# Revit family: Casement_41_G_Top_Hung_SD_Standard
name_source: partatom
category: Windows
revit_build: Autodesk Revit 2014 (Build: 20130308_1515(x64)
units: mm (PartAtom-declared; Revit-internal decimal feet)

## types (12) — shared parameters
Corrected Mullion Configuration = 2 mm  [stored 0.00656168 ft]
Custom Window Height = 1190 mm  [stored 3.9042 ft]
Description = Window 41mm, Type G, Top hung, Standard sash
Frame Profile Thickness = 41 mm  [stored 0.134514 ft]
Heavy Duty Sash = No
Limit Fixed Pane Height Max = 3000 mm  [stored 9.84252 ft]
Limit Fixed Pane Height Min = 200 mm  [stored 0.656168 ft]
Limit Fixed Pane Width Max = 3000 mm  [stored 9.84252 ft]
Limit Fixed Pane Width Min = 200 mm  [stored 0.656168 ft]
Limit Sash Height Max = 1200 mm  [stored 3.93701 ft]
Limit Sash Height Min = 300 mm  [stored 0.984252 ft]
Limit Sash Width Max = 1500 mm  [stored 4.92126 ft]
Limit Sash Width Min = 300 mm  [stored 0.984252 ft]
Manufacturer = Crealco
Max System DG Unit Thickness = 25 mm  [stored 0.082021 ft]
Model = Casement 41
Rough Width = 3 mm  [stored 0.00984252 ft]
Sash Side Gap = 44 mm
Standard Mullion Different = No
Standard Sash = Yes
URL = http://www.crealco.co.za
Wall Closure = By host
zero-valued in all types: Custom Frame Offset From Exterior

## per-type parameters (varying)
| type | Clearvue Insulated LowE SHGC Value | Clearvue Insulated LowE U Value | Clearvue Insulated SHGC Value | Clearvue Insulated U Value | Clearvue SHGC Value | Clearvue U Value | Custom Sash Width | Custom Windload | Custom Window Width | Energy Advantage SHGC Value | Energy Advantage U Value | Intruderprufe Insulated LowE SHGC Value | Intruderprufe Insulated LowE U Value | Intruderprufe Insulated SHGC Value | Intruderprufe Insulated U Value | Intruderprufe LowE SHGC Value | Intruderprufe LowE U Value | Intruderprufe SHGC Value | Intruderprufe U Value | Toughened Safety SHGC Value | Toughened Safety U Value |
| 41-1212DT-SD-1000Pa | 0.72 | 4.3 | 0.72 | 4.38 | 0.545 | 6.06 | 525 mm | 1000 mm  [stored 3.28084 ft] | 1190 mm  [stored 3.9042 ft] | 0.489 | 4.71 | 0.598 | 3.11 | 0.599 | 3.31 | 0.455 | 4.57 | 0.513 | 5.78 | 0.545 | 6.06 |
| 41-1212DT-SD-1500Pa | 0.72 | 4.3 | 0.72 | 4.38 | 0.545 | 6.06 | 525 mm | 1500 mm  [stored 4.92126 ft] | 1190 mm  [stored 3.9042 ft] | 0.489 | 4.71 | 0.598 | 3.11 | 0.599 | 3.31 | 0.455 | 4.57 | 0.513 | 5.78 | 0.545 | 6.06 |
| 41-1212DT-SD-2000Pa | 0.72 | 4.3 | 0.72 | 4.38 | 0.545 | 6.06 | 525 mm | 2000 mm  [stored 6.56168 ft] | 1190 mm  [stored 3.9042 ft] | 0.489 | 4.71 | 0.598 | 3.11 | 0.599 | 3.31 | 0.455 | 4.57 | 0.513 | 5.78 | 0.545 | 6.06 |
| 41-1512DT-SD-1000Pa | 0.746 | 4.49 | 0.746 | 4.55 | 0.591 | 6.04 | 525 mm | 1000 mm  [stored 3.28084 ft] | 1490 mm  [stored 4.88845 ft] | 0.53 | 4.58 | 0.62 | 3.13 | 0.62 | 3.3 | 0.492 | 4.43 | 0.556 | 5.77 | 0.591 | 6.04 |
| 41-1512DT-SD-1500Pa | 0.746 | 4.49 | 0.746 | 4.55 | 0.591 | 6.04 | 525 mm | 1500 mm  [stored 4.92126 ft] | 1490 mm  [stored 4.88845 ft] | 0.53 | 4.58 | 0.62 | 3.13 | 0.62 | 3.3 | 0.492 | 4.43 | 0.556 | 5.77 | 0.591 | 6.04 |
| 41-1512DT-SD-2000Pa | 0.746 | 4.49 | 0.746 | 4.55 | 0.591 | 6.04 | 525 mm | 2000 mm  [stored 6.56168 ft] | 1490 mm  [stored 4.88845 ft] | 0.53 | 4.58 | 0.62 | 3.13 | 0.62 | 3.3 | 0.492 | 4.43 | 0.556 | 5.77 | 0.591 | 6.04 |
| 41-1812DT-SD-1000Pa | 0.747 | 4.52 | 0.747 | 4.57 | 0.595 | 6.04 | 825 mm | 1000 mm  [stored 3.28084 ft] | 1790 mm  [stored 5.8727 ft] | 0.533 | 4.52 | 0.62 | 3.13 | 0.621 | 3.34 | 0.496 | 4.39 | 0.56 | 5.75 | 0.595 | 6.04 |
| 41-1812DT-SD-1500Pa | 0.747 | 4.52 | 0.747 | 4.57 | 0.595 | 6.04 | 825 mm | 1500 mm  [stored 4.92126 ft] | 1790 mm  [stored 5.8727 ft] | 0.533 | 4.52 | 0.62 | 3.13 | 0.621 | 3.34 | 0.496 | 4.39 | 0.56 | 5.75 | 0.595 | 6.04 |
| 41-1812DT-SD-2000Pa | 0.747 | 4.52 | 0.747 | 4.57 | 0.595 | 6.04 | 825 mm | 2000 mm  [stored 6.56168 ft] | 1790 mm  [stored 5.8727 ft] | 0.533 | 4.52 | 0.62 | 3.13 | 0.621 | 3.34 | 0.496 | 4.39 | 0.56 | 5.75 | 0.595 | 6.04 |
| 41-2412DT-SD-1000Pa | 0.773 | 4.7 | 0.773 | 4.74 | 0.639 | 6.02 | 825 mm | 1000 mm  [stored 3.28084 ft] | 2390 mm  [stored 7.84121 ft] | 0.572 | 4.4 | 0.641 | 3.16 | 0.642 | 3.32 | 0.532 | 4.26 | 0.601 | 5.75 | 0.639 | 6.02 |
| 41-2412DT-SD-1500Pa | 0.773 | 4.7 | 0.773 | 4.74 | 0.639 | 6.02 | 825 mm | 1500 mm  [stored 4.92126 ft] | 2390 mm  [stored 7.84121 ft] | 0.572 | 4.4 | 0.641 | 3.16 | 0.642 | 3.32 | 0.532 | 4.26 | 0.601 | 5.75 | 0.639 | 6.02 |
| 41-2412DT-SD-2000Pa | 0.773 | 4.7 | 0.773 | 4.74 | 0.639 | 6.02 | 825 mm | 2000 mm  [stored 6.56168 ft] | 2390 mm  [stored 7.84121 ft] | 0.572 | 4.4 | 0.641 | 3.16 | 0.642 | 3.32 | 0.532 | 4.26 | 0.601 | 5.75 | 0.639 | 6.02 |

note: [stored X ft] marks values corroborated as IEEE doubles in the binary element streams (Revit-internal decimal feet)

## geometry (parser evidence)
native form markers: Sweep x15
no freeform markers — native parametric forms only
